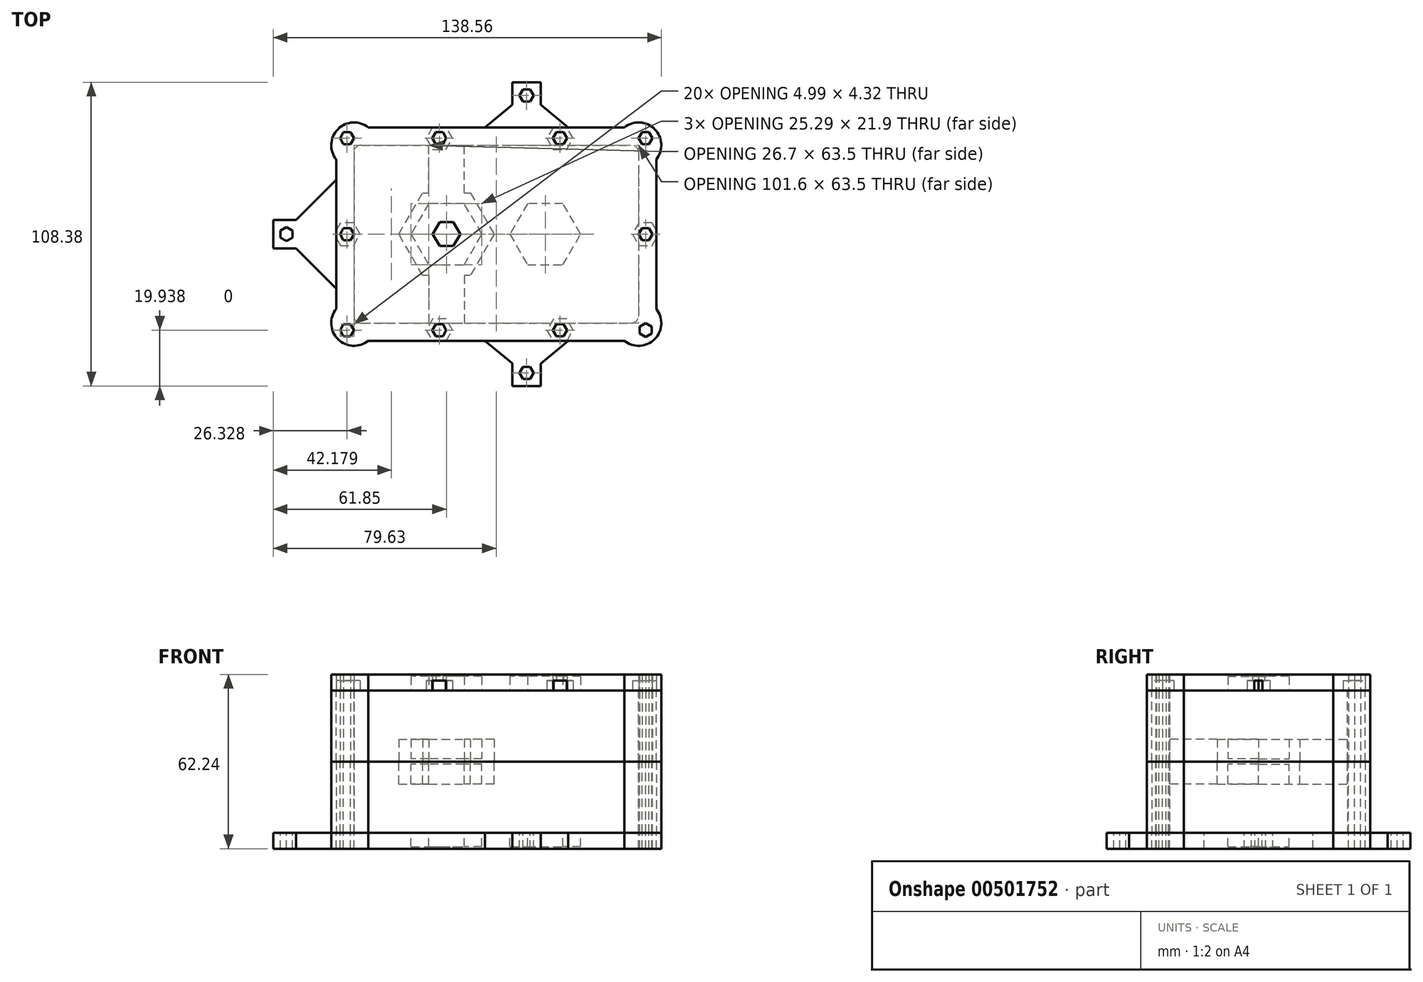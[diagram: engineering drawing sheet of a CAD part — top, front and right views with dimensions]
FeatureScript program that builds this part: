
annotation { "Feature Type Name" : "Feature", "Feature Type Description" : "" }
export const myFeature = defineFeature(function(context is Context, id is Id, definition is map)
    precondition{}
    {
        {
            var Q0;
            Q0=qCreatedBy(makeId("Top.planeOp"),FACE);
            var sketch = newSketch(context, id + "F0", { "sketchPlane" : qUnion([Q0])});
            skLineSegment(sketch, "E0.bottom", {"start": v(-48.26, 31.75) * mm, "end": v(48.26, 31.75) * mm});
            skLineSegment(sketch, "E0.top", {"start": v(-48.26, -31.75) * mm, "end": v(48.26, -31.75) * mm});
            skLineSegment(sketch, "E0.left", {"start": v(-50.8, 29.21) * mm, "end": v(-50.8, -29.21) * mm});
            skLineSegment(sketch, "E0.right", {"start": v(50.8, 29.21) * mm, "end": v(50.8, -29.21) * mm});
            skLineSegment(sketch, "E1", {"start": v(0, 0) * mm, "end": v(0, 31.75) * mm, "construction": true});
            skLineSegment(sketch, "E2", {"start": v(0, 0) * mm, "end": v(-50.8, 0) * mm, "construction": true});
            skLineSegment(sketch, "E3.0", {"start": v(57.15, 26.68) * mm, "end": v(57.15, -26.68) * mm});
            skLineSegment(sketch, "E3.1", {"start": v(-45.73, 38.1) * mm, "end": v(45.73, 38.1) * mm});
            skLineSegment(sketch, "E3.2", {"start": v(-57.15, 26.68) * mm, "end": v(-57.15, -26.68) * mm});
            skLineSegment(sketch, "E3.3", {"start": v(-45.73, -38.1) * mm, "end": v(45.73, -38.1) * mm});
            skPoint(sketch, "E4.visualSharp", {"position": v(-50.8, 31.75) * mm});
            skArc(sketch, "E4.filletArc", {"start": v(-48.26, 31.75) * mm, "mid": v(-50.06, 31) * mm, "end": v(-50.8, 29.21) * mm});
            skPoint(sketch, "E5.visualSharp", {"position": v(-57.15, 38.1) * mm});
            skPoint(sketch, "E6.visualSharp", {"position": v(50.8, 31.75) * mm});
            skArc(sketch, "E6.filletArc", {"start": v(50.8, 29.21) * mm, "mid": v(50.06, 31) * mm, "end": v(48.26, 31.75) * mm});
            skPoint(sketch, "E7.visualSharp", {"position": v(57.15, 38.1) * mm});
            skPoint(sketch, "E8.visualSharp", {"position": v(57.15, -38.1) * mm});
            skPoint(sketch, "E9.visualSharp", {"position": v(50.8, -31.75) * mm});
            skArc(sketch, "E9.filletArc", {"start": v(48.26, -31.75) * mm, "mid": v(50.06, -31) * mm, "end": v(50.8, -29.21) * mm});
            skPoint(sketch, "E10.visualSharp", {"position": v(-50.8, -31.75) * mm});
            skArc(sketch, "E10.filletArc", {"start": v(-50.8, -29.21) * mm, "mid": v(-50.06, -31) * mm, "end": v(-48.26, -31.75) * mm});
            skPoint(sketch, "E11.visualSharp", {"position": v(-57.15, -38.1) * mm});
            skArc(sketch, "E12", {"start": v(-57.15, -26.68) * mm, "mid": v(-56.55, -37.5) * mm, "end": v(-45.73, -38.1) * mm});
            skArc(sketch, "E13", {"start": v(45.73, -38.1) * mm, "mid": v(56.55, -37.5) * mm, "end": v(57.15, -26.68) * mm});
            skArc(sketch, "E14", {"start": v(57.15, 26.68) * mm, "mid": v(56.55, 37.5) * mm, "end": v(45.73, 38.1) * mm});
            skArc(sketch, "E15", {"start": v(-45.73, 38.1) * mm, "mid": v(-56.55, 37.5) * mm, "end": v(-57.15, 26.68) * mm});
            skSolve(sketch);
        }
        {
            var Q0;
            Q0=makeQuery(id+"F0.imprint","IMPRINT",FACE,{"disambiguationData":[TD([[makeQuery(id+"F0.imprint","IMPRINT",EDGE,{"derivedFrom":sQuery(id+"F0.wireOp",EDGE,"E0.bottom")}),1.0]])]});
            var Q1;
            {var subQ0=sQuery(id+"F0.wireOp",EDGE,"E11.filletArc");Q1=makeQuery(id+"F0.imprint","IMPRINT",FACE,{"disambiguationData":[TD([[makeQuery(id+"F0.imprint","IMPRINT",EDGE,{"derivedFrom":subQ0}),-1.0]])]});}
            var Q2;
            {var subQ0=sQuery(id+"F0.wireOp",EDGE,"E8.filletArc");Q2=makeQuery(id+"F0.imprint","IMPRINT",FACE,{"disambiguationData":[TD([[makeQuery(id+"F0.imprint","IMPRINT",EDGE,{"derivedFrom":subQ0}),-1.0]])]});}
            var Q3;
            {var subQ0=sQuery(id+"F0.wireOp",EDGE,"E7.filletArc");Q3=makeQuery(id+"F0.imprint","IMPRINT",FACE,{"disambiguationData":[TD([[makeQuery(id+"F0.imprint","IMPRINT",EDGE,{"derivedFrom":subQ0}),-1.0]])]});}
            var Q4;
            {var subQ0=sQuery(id+"F0.wireOp",EDGE,"E5.filletArc");Q4=makeQuery(id+"F0.imprint","IMPRINT",FACE,{"disambiguationData":[TD([[makeQuery(id+"F0.imprint","IMPRINT",EDGE,{"derivedFrom":subQ0}),-1.0]])]});}
            extrude(context, id + "F1", {"entities" : qUnion([Q0, Q1, Q2, Q3, Q4]), "depth" : 25.4 * mm});
        }
        {
            var Q0;
            Q0=makeQuery(id+"F1.opExtrude","CAP_FACE",FACE,{"disambiguationData":[OSD([sQuery(id+"F0.wireOp",EDGE,"E0.bottom"),sQuery(id+"F0.wireOp",EDGE,"E0.top"),sQuery(id+"F0.wireOp",EDGE,"E0.left"),sQuery(id+"F0.wireOp",EDGE,"E0.right"),sQuery(id+"F0.wireOp",EDGE,"E3.0"),sQuery(id+"F0.wireOp",EDGE,"E3.1"),sQuery(id+"F0.wireOp",EDGE,"E3.2"),sQuery(id+"F0.wireOp",EDGE,"E3.3"),sQuery(id+"F0.wireOp",EDGE,"E4.filletArc"),sQuery(id+"F0.wireOp",EDGE,"E5.filletArc"),sQuery(id+"F0.wireOp",EDGE,"E6.filletArc"),sQuery(id+"F0.wireOp",EDGE,"E7.filletArc"),sQuery(id+"F0.wireOp",EDGE,"E8.filletArc"),sQuery(id+"F0.wireOp",EDGE,"E9.filletArc"),sQuery(id+"F0.wireOp",EDGE,"E10.filletArc"),sQuery(id+"F0.wireOp",EDGE,"E11.filletArc")])],"isStart":true});
            var sketch = newSketch(context, id + "F2", { "sketchPlane" : qUnion([Q0])});
            skCircle(sketch, "E16", {"center": v(-17.78, 0) * mm, "radius": 57.15 * mm, "construction": true});
            skLineSegment(sketch, "E17", {"start": v(-17.78, 0) * mm, "end": v(10.8, -49.5) * mm, "construction": true});
            skLineSegment(sketch, "E18", {"start": v(-17.78, 0) * mm, "end": v(10.8, 49.5) * mm, "construction": true});
            skLineSegment(sketch, "E19", {"start": v(-17.78, 0) * mm, "end": v(-74.93, 0) * mm, "construction": true});
            skCircle(sketch, "E20.cCircle", {"center": v(-17.78, 0) * mm, "radius": 4.25 * mm, "construction": true});
            skLineSegment(sketch, "E20.0", {"start": v(-20.23, 4.25) * mm, "end": v(-15.33, 4.25) * mm});
            skLineSegment(sketch, "E20.1", {"start": v(-15.33, 4.25) * mm, "end": v(-12.87, 0) * mm});
            skLineSegment(sketch, "E20.2", {"start": v(-12.87, 0) * mm, "end": v(-15.33, -4.25) * mm});
            skLineSegment(sketch, "E20.3", {"start": v(-15.33, -4.25) * mm, "end": v(-20.23, -4.25) * mm});
            skLineSegment(sketch, "E20.4", {"start": v(-20.23, -4.25) * mm, "end": v(-22.69, 0) * mm});
            skLineSegment(sketch, "E20.5", {"start": v(-22.69, 0) * mm, "end": v(-20.23, 4.25) * mm});
            skPoint(sketch, "E20.0.midPoint", {"position": v(-17.78, 4.25) * mm});
            skCircle(sketch, "E21.cCircle", {"center": v(-74.93, 0) * mm, "radius": 2.16 * mm, "construction": true});
            skLineSegment(sketch, "E21.0", {"start": v(-77.09, -1.25) * mm, "end": v(-77.09, 1.25) * mm});
            skLineSegment(sketch, "E21.1", {"start": v(-77.09, 1.25) * mm, "end": v(-74.93, 2.5) * mm});
            skLineSegment(sketch, "E21.2", {"start": v(-74.93, 2.5) * mm, "end": v(-72.77, 1.25) * mm});
            skLineSegment(sketch, "E21.3", {"start": v(-72.77, 1.25) * mm, "end": v(-72.77, -1.25) * mm});
            skLineSegment(sketch, "E21.4", {"start": v(-72.77, -1.25) * mm, "end": v(-74.93, -2.5) * mm});
            skLineSegment(sketch, "E21.5", {"start": v(-74.93, -2.5) * mm, "end": v(-77.09, -1.25) * mm});
            skPoint(sketch, "E21.0.midPoint", {"position": v(-77.09, 0) * mm});
            skPoint(sketch, "E22", {"position": v(-57.15, 0) * mm});
            skCircle(sketch, "E23.cCircle", {"center": v(10.8, 49.5) * mm, "radius": 2.16 * mm, "construction": true});
            skLineSegment(sketch, "E23.0", {"start": v(9.55, 51.65) * mm, "end": v(12.04, 51.65) * mm});
            skLineSegment(sketch, "E23.1", {"start": v(12.04, 51.65) * mm, "end": v(13.29, 49.5) * mm});
            skLineSegment(sketch, "E23.2", {"start": v(13.29, 49.5) * mm, "end": v(12.04, 47.33) * mm});
            skLineSegment(sketch, "E23.3", {"start": v(12.04, 47.33) * mm, "end": v(9.55, 47.33) * mm});
            skLineSegment(sketch, "E23.4", {"start": v(9.55, 47.33) * mm, "end": v(8.3, 49.5) * mm});
            skLineSegment(sketch, "E23.5", {"start": v(8.3, 49.5) * mm, "end": v(9.55, 51.65) * mm});
            skPoint(sketch, "E23.0.midPoint", {"position": v(10.8, 51.65) * mm});
            skCircle(sketch, "E24.cCircle", {"center": v(10.8, -49.5) * mm, "radius": 2.16 * mm, "construction": true});
            skLineSegment(sketch, "E24.0", {"start": v(12.04, -51.65) * mm, "end": v(9.55, -51.65) * mm});
            skLineSegment(sketch, "E24.1", {"start": v(9.55, -51.65) * mm, "end": v(8.3, -49.5) * mm});
            skLineSegment(sketch, "E24.2", {"start": v(8.3, -49.5) * mm, "end": v(9.55, -47.33) * mm});
            skLineSegment(sketch, "E24.3", {"start": v(9.55, -47.33) * mm, "end": v(12.04, -47.33) * mm});
            skLineSegment(sketch, "E24.4", {"start": v(12.04, -47.33) * mm, "end": v(13.29, -49.5) * mm});
            skLineSegment(sketch, "E24.5", {"start": v(13.29, -49.5) * mm, "end": v(12.04, -51.65) * mm});
            skPoint(sketch, "E24.0.midPoint", {"position": v(10.8, -51.65) * mm});
            skLineSegment(sketch, "E25.bottom", {"start": v(-79.63, -5.08) * mm, "end": v(-57.15, -5.08) * mm});
            skLineSegment(sketch, "E25.top", {"start": v(-79.63, 5.08) * mm, "end": v(-57.15, 5.08) * mm});
            skLineSegment(sketch, "E25.left", {"start": v(-79.63, -5.08) * mm, "end": v(-79.63, 5.08) * mm});
            skLineSegment(sketch, "E25.right", {"start": v(-57.15, -5.08) * mm, "end": v(-57.15, 5.08) * mm});
            skLineSegment(sketch, "E26.bottom", {"start": v(5.71, -54.2) * mm, "end": v(15.87, -54.2) * mm});
            skLineSegment(sketch, "E26.top", {"start": v(5.71, -38.1) * mm, "end": v(15.87, -38.1) * mm});
            skLineSegment(sketch, "E26.left", {"start": v(5.71, -54.2) * mm, "end": v(5.71, -38.1) * mm});
            skLineSegment(sketch, "E26.right", {"start": v(15.87, -54.2) * mm, "end": v(15.87, -38.1) * mm});
            skLineSegment(sketch, "E27.bottom", {"start": v(5.72, 38.1) * mm, "end": v(15.88, 38.1) * mm});
            skLineSegment(sketch, "E27.top", {"start": v(5.72, 54.2) * mm, "end": v(15.88, 54.2) * mm});
            skLineSegment(sketch, "E27.left", {"start": v(5.72, 38.1) * mm, "end": v(5.72, 54.2) * mm});
            skLineSegment(sketch, "E27.right", {"start": v(15.88, 38.1) * mm, "end": v(15.88, 54.2) * mm});
            skLineSegment(sketch, "E28", {"start": v(10.8, 49.5) * mm, "end": v(10.8, 54.2) * mm, "construction": true});
            skLineSegment(sketch, "E29", {"start": v(10.8, -54.2) * mm, "end": v(10.8, -49.5) * mm, "construction": true});
            skLineSegment(sketch, "E30", {"start": v(-79.63, 0) * mm, "end": v(-77.09, 0) * mm, "construction": true});
            skLineSegment(sketch, "E31", {"start": v(5.72, 46.15) * mm, "end": v(-4.11, 38.1) * mm});
            skLineSegment(sketch, "E32", {"start": v(15.88, 46.19) * mm, "end": v(25.67, 38.1) * mm});
            skPoint(sketch, "E33", {"position": v(15.88, 46.15) * mm});
            skLineSegment(sketch, "E34", {"start": v(15.87, -46.15) * mm, "end": v(25.7, -38.1) * mm});
            skLineSegment(sketch, "E35", {"start": v(5.71, -46.15) * mm, "end": v(-4.11, -38.1) * mm});
            skLineSegment(sketch, "E36", {"start": v(-71.52, -5.08) * mm, "end": v(-57.15, -19.45) * mm});
            skLineSegment(sketch, "E37", {"start": v(-71.52, 5.08) * mm, "end": v(-57.15, 19.45) * mm});
            skCircle(sketch, "E38.cCircle", {"center": v(17.5, 0) * mm, "radius": 4.25 * mm, "construction": true});
            skLineSegment(sketch, "E38.0", {"start": v(15.04, 4.25) * mm, "end": v(19.95, 4.25) * mm});
            skLineSegment(sketch, "E38.1", {"start": v(19.95, 4.25) * mm, "end": v(22.4, 0) * mm});
            skLineSegment(sketch, "E38.2", {"start": v(22.4, 0) * mm, "end": v(19.95, -4.25) * mm});
            skLineSegment(sketch, "E38.3", {"start": v(19.95, -4.25) * mm, "end": v(15.04, -4.25) * mm});
            skLineSegment(sketch, "E38.4", {"start": v(15.04, -4.25) * mm, "end": v(12.59, 0) * mm});
            skLineSegment(sketch, "E38.5", {"start": v(12.59, 0) * mm, "end": v(15.04, 4.25) * mm});
            skPoint(sketch, "E38.0.midPoint", {"position": v(17.5, 4.25) * mm});
            skSolve(sketch);
        }
        {
            var Q0;
            {var subQ3=sQuery(id+"F2.wireOp",EDGE,"E37");Q0=makeQuery(id+"F2.imprint","IMPRINT",FACE,{"disambiguationData":[TD([[makeQuery(id+"F2.imprint","IMPRINT",EDGE,{"derivedFrom":subQ3}),-1.0]])]});}
            var Q1;
            Q1=makeQuery(id+"F2.imprint","IMPRINT",FACE,{"disambiguationData":[TD([[makeQuery(id+"F2.imprint","IMPRINT",EDGE,{"derivedFrom":sQuery(id+"F2.wireOp",EDGE,"E21.0")}),1.0]])]});
            var Q2;
            {var subQ3=sQuery(id+"F2.wireOp",EDGE,"E36");Q2=makeQuery(id+"F2.imprint","IMPRINT",FACE,{"disambiguationData":[TD([[makeQuery(id+"F2.imprint","IMPRINT",EDGE,{"derivedFrom":subQ3}),1.0]])]});}
            var Q3;
            {var subQ14=sQuery(id+"F2.wireOp",EDGE,"E25.right");Q3=makeQuery(id+"F2.imprint","IMPRINT",FACE,{"disambiguationData":[TD([[makeQuery(id+"F2.imprint","IMPRINT",EDGE,{"derivedFrom":subQ14}),-1.0]])]});}
            var Q4;
            Q4=makeQuery(id+"F2.imprint","IMPRINT",FACE,{"disambiguationData":[TD([[makeQuery(id+"F2.imprint","IMPRINT",EDGE,{"derivedFrom":sQuery(id+"F2.wireOp",EDGE,"E20.0")}),1.0]])]});
            var Q5;
            Q5=makeQuery(id+"F2.imprint","IMPRINT",FACE,{"disambiguationData":[TD([[makeQuery(id+"F2.imprint","IMPRINT",EDGE,{"derivedFrom":sQuery(id+"F2.wireOp",EDGE,"E23.0")}),1.0]])]});
            var Q6;
            {var subQ3=sQuery(id+"F2.wireOp",EDGE,"E31");Q6=makeQuery(id+"F2.imprint","IMPRINT",FACE,{"disambiguationData":[TD([[makeQuery(id+"F2.imprint","IMPRINT",EDGE,{"derivedFrom":subQ3}),1.0]])]});}
            var Q7;
            {var subQ3=sQuery(id+"F2.wireOp",EDGE,"E32");Q7=makeQuery(id+"F2.imprint","IMPRINT",FACE,{"disambiguationData":[TD([[makeQuery(id+"F2.imprint","IMPRINT",EDGE,{"derivedFrom":subQ3}),-1.0]])]});}
            var Q8;
            {var subQ3=sQuery(id+"F2.wireOp",EDGE,"E35");Q8=makeQuery(id+"F2.imprint","IMPRINT",FACE,{"disambiguationData":[TD([[makeQuery(id+"F2.imprint","IMPRINT",EDGE,{"derivedFrom":subQ3}),-1.0]])]});}
            var Q9;
            Q9=makeQuery(id+"F2.imprint","IMPRINT",FACE,{"disambiguationData":[TD([[makeQuery(id+"F2.imprint","IMPRINT",EDGE,{"derivedFrom":sQuery(id+"F2.wireOp",EDGE,"E24.0")}),1.0]])]});
            var Q10;
            {var subQ3=sQuery(id+"F2.wireOp",EDGE,"E34");Q10=makeQuery(id+"F2.imprint","IMPRINT",FACE,{"disambiguationData":[TD([[makeQuery(id+"F2.imprint","IMPRINT",EDGE,{"derivedFrom":subQ3}),1.0]])]});}
            var Q11;
            Q11=makeQuery(id+"F2.imprint","IMPRINT",FACE,{"disambiguationData":[TD([[makeQuery(id+"F2.imprint","IMPRINT",EDGE,{"derivedFrom":sQuery(id+"F2.wireOp",EDGE,"E38.0")}),-1.0]])]});
            extrude(context, id + "F3", {"entities" : qUnion([Q0, Q1, Q2, Q3, Q4, Q5, Q6, Q7, Q8, Q9, Q10, Q11]), "depth" : 5.7 * mm});
        }
        {
            var Q0;
            {var subQ0=sQuery(id+"F2.wireOp",EDGE,"E20.0");var subQ1=sQuery(id+"F2.wireOp",EDGE,"E38.5");var subQ2=sQuery(id+"F2.wireOp",EDGE,"E20.4");var subQ3=sQuery(id+"F2.wireOp",EDGE,"E20.5");var subQ4=sQuery(id+"F2.wireOp",EDGE,"E38.1");var subQ5=sQuery(id+"F2.wireOp",EDGE,"E38.4");var subQ6=sQuery(id+"F2.wireOp",EDGE,"E20.1");var subQ7=sQuery(id+"F2.wireOp",EDGE,"E20.2");var subQ8=sQuery(id+"F2.wireOp",EDGE,"E20.3");var subQ9=sQuery(id+"F2.wireOp",EDGE,"E38.0");var subQ10=sQuery(id+"F2.wireOp",EDGE,"E38.2");var subQ11=sQuery(id+"F2.wireOp",EDGE,"E38.3");Q0=makeQuery(id+"F3.boolean.opBoolean","SPLIT",FACE,{"disambiguationData":[TD([makeQuery(id+"F1.opExtrude","SWEPT_FACE",FACE,{"disambiguationData":[OSD([sQuery(id+"F0.wireOp",EDGE,"E0.bottom")])]})])],"derivedFrom":makeQuery(id+"F3.opExtrude","CAP_FACE",FACE,{"disambiguationData":[OSD([sQuery(id+"F0.wireOp",EDGE,"E3.0"),sQuery(id+"F0.wireOp",EDGE,"E3.1"),sQuery(id+"F0.wireOp",EDGE,"E3.2"),sQuery(id+"F0.wireOp",EDGE,"E3.3"),sQuery(id+"F0.wireOp",EDGE,"E12"),sQuery(id+"F0.wireOp",EDGE,"E13"),sQuery(id+"F0.wireOp",EDGE,"E14"),sQuery(id+"F0.wireOp",EDGE,"E15"),subQ0,subQ6,subQ7,subQ8,subQ2,subQ3,sQuery(id+"F2.wireOp",EDGE,"E21.0"),sQuery(id+"F2.wireOp",EDGE,"E21.1"),sQuery(id+"F2.wireOp",EDGE,"E21.2"),sQuery(id+"F2.wireOp",EDGE,"E21.3"),sQuery(id+"F2.wireOp",EDGE,"E21.4"),sQuery(id+"F2.wireOp",EDGE,"E21.5"),sQuery(id+"F2.wireOp",EDGE,"E23.0"),sQuery(id+"F2.wireOp",EDGE,"E23.1"),sQuery(id+"F2.wireOp",EDGE,"E23.2"),sQuery(id+"F2.wireOp",EDGE,"E23.3"),sQuery(id+"F2.wireOp",EDGE,"E23.4"),sQuery(id+"F2.wireOp",EDGE,"E23.5"),sQuery(id+"F2.wireOp",EDGE,"E24.0"),sQuery(id+"F2.wireOp",EDGE,"E24.1"),sQuery(id+"F2.wireOp",EDGE,"E24.2"),sQuery(id+"F2.wireOp",EDGE,"E24.3"),sQuery(id+"F2.wireOp",EDGE,"E24.4"),sQuery(id+"F2.wireOp",EDGE,"E24.5"),sQuery(id+"F2.wireOp",EDGE,"E25.bottom"),sQuery(id+"F2.wireOp",EDGE,"E25.top"),sQuery(id+"F2.wireOp",EDGE,"E25.left"),sQuery(id+"F2.wireOp",EDGE,"E26.bottom"),sQuery(id+"F2.wireOp",EDGE,"E26.left"),sQuery(id+"F2.wireOp",EDGE,"E26.right"),sQuery(id+"F2.wireOp",EDGE,"E27.top"),sQuery(id+"F2.wireOp",EDGE,"E27.left"),sQuery(id+"F2.wireOp",EDGE,"E27.right"),sQuery(id+"F2.wireOp",EDGE,"E31"),sQuery(id+"F2.wireOp",EDGE,"E32"),sQuery(id+"F2.wireOp",EDGE,"E34"),sQuery(id+"F2.wireOp",EDGE,"E35"),sQuery(id+"F2.wireOp",EDGE,"E36"),sQuery(id+"F2.wireOp",EDGE,"E37"),subQ9,subQ4,subQ10,subQ11,subQ5,subQ1])],"isStart":true})});}
            var sketch = newSketch(context, id + "F4", { "sketchPlane" : qUnion([Q0])});
            skPoint(sketch, "E39.0", {"position": v(-17.78, 0) * mm});
            skPoint(sketch, "E39.1", {"position": v(17.5, 0) * mm});
            skCircle(sketch, "E40.cCircle", {"center": v(-17.78, 0) * mm, "radius": 10.95 * mm, "construction": true});
            skLineSegment(sketch, "E40.0", {"start": v(-24.1, 10.95) * mm, "end": v(-11.46, 10.95) * mm});
            skLineSegment(sketch, "E40.1", {"start": v(-11.46, 10.95) * mm, "end": v(-5.14, 0) * mm});
            skLineSegment(sketch, "E40.2", {"start": v(-5.14, 0) * mm, "end": v(-11.46, -10.95) * mm});
            skLineSegment(sketch, "E40.3", {"start": v(-11.46, -10.95) * mm, "end": v(-24.1, -10.95) * mm});
            skLineSegment(sketch, "E40.4", {"start": v(-24.1, -10.95) * mm, "end": v(-30.42, 0) * mm});
            skLineSegment(sketch, "E40.5", {"start": v(-30.42, 0) * mm, "end": v(-24.1, 10.95) * mm});
            skPoint(sketch, "E40.0.midPoint", {"position": v(-17.78, 10.95) * mm});
            skCircle(sketch, "E41.cCircle", {"center": v(17.5, 0) * mm, "radius": 10.95 * mm, "construction": true});
            skLineSegment(sketch, "E41.0", {"start": v(11.17, 10.95) * mm, "end": v(23.82, 10.95) * mm});
            skLineSegment(sketch, "E41.1", {"start": v(23.82, 10.95) * mm, "end": v(30.14, 0) * mm});
            skLineSegment(sketch, "E41.2", {"start": v(30.14, 0) * mm, "end": v(23.82, -10.95) * mm});
            skLineSegment(sketch, "E41.3", {"start": v(23.82, -10.95) * mm, "end": v(11.17, -10.95) * mm});
            skLineSegment(sketch, "E41.4", {"start": v(11.17, -10.95) * mm, "end": v(4.85, 0) * mm});
            skLineSegment(sketch, "E41.5", {"start": v(4.85, 0) * mm, "end": v(11.17, 10.95) * mm});
            skPoint(sketch, "E41.0.midPoint", {"position": v(17.5, 10.95) * mm});
            skSolve(sketch);
        }
        {
            var Q0;
            Q0=makeQuery(id+"F4.imprint","IMPRINT",FACE,{"disambiguationData":[TD([[makeQuery(id+"F4.imprint","IMPRINT",EDGE,{"derivedFrom":sQuery(id+"F4.wireOp",EDGE,"E40.0")}),-1.0]])]});
            var Q1;
            Q1=makeQuery(id+"F4.imprint","IMPRINT",FACE,{"disambiguationData":[TD([[makeQuery(id+"F4.imprint","IMPRINT",EDGE,{"derivedFrom":sQuery(id+"F4.wireOp",EDGE,"E41.0")}),-1.0]])]});
            extrude(context, id + "F5", {"entities" : qUnion([Q0, Q1]), "operationType" : NewBodyOperationType.REMOVE, "oppositeDirection" : true, "depth" : 5 * mm});
        }
        {
            var Q0;
            Q0=makeQuery(id+"F1.opExtrude","CAP_FACE",FACE,{"disambiguationData":[OSD([sQuery(id+"F0.wireOp",EDGE,"E0.bottom"),sQuery(id+"F0.wireOp",EDGE,"E0.top"),sQuery(id+"F0.wireOp",EDGE,"E0.left"),sQuery(id+"F0.wireOp",EDGE,"E0.right"),sQuery(id+"F0.wireOp",EDGE,"E3.0"),sQuery(id+"F0.wireOp",EDGE,"E3.1"),sQuery(id+"F0.wireOp",EDGE,"E3.2"),sQuery(id+"F0.wireOp",EDGE,"E3.3"),sQuery(id+"F0.wireOp",EDGE,"E4.filletArc"),sQuery(id+"F0.wireOp",EDGE,"E6.filletArc"),sQuery(id+"F0.wireOp",EDGE,"E9.filletArc"),sQuery(id+"F0.wireOp",EDGE,"E10.filletArc"),sQuery(id+"F0.wireOp",EDGE,"E12"),sQuery(id+"F0.wireOp",EDGE,"E13"),sQuery(id+"F0.wireOp",EDGE,"E14"),sQuery(id+"F0.wireOp",EDGE,"E15")])],"isStart":false});
            var sketch = newSketch(context, id + "F6", { "sketchPlane" : qUnion([Q0])});
            skLineSegment(sketch, "E42", {"start": v(-56.55, 37.5) * mm, "end": v(-50.06, 31) * mm, "construction": true});
            skLineSegment(sketch, "E43", {"start": v(50.06, 31) * mm, "end": v(56.55, 37.5) * mm, "construction": true});
            skLineSegment(sketch, "E44", {"start": v(56.55, -37.5) * mm, "end": v(50.06, -31) * mm, "construction": true});
            skLineSegment(sketch, "E45", {"start": v(-50.06, -31) * mm, "end": v(-56.55, -37.5) * mm, "construction": true});
            skCircle(sketch, "E46.cCircle", {"center": v(-53.3, 34.25) * mm, "radius": 2.16 * mm, "construction": true});
            skLineSegment(sketch, "E46.0", {"start": v(-54.55, 36.41) * mm, "end": v(-52.06, 36.41) * mm});
            skLineSegment(sketch, "E46.1", {"start": v(-52.06, 36.41) * mm, "end": v(-50.8, 34.25) * mm});
            skLineSegment(sketch, "E46.2", {"start": v(-50.8, 34.25) * mm, "end": v(-52.06, 32.1) * mm});
            skLineSegment(sketch, "E46.3", {"start": v(-52.06, 32.1) * mm, "end": v(-54.55, 32.1) * mm});
            skLineSegment(sketch, "E46.4", {"start": v(-54.55, 32.1) * mm, "end": v(-55.8, 34.25) * mm});
            skLineSegment(sketch, "E46.5", {"start": v(-55.8, 34.25) * mm, "end": v(-54.55, 36.41) * mm});
            skPoint(sketch, "E46.0.midPoint", {"position": v(-53.3, 36.41) * mm});
            skCircle(sketch, "E47.cCircle", {"center": v(53.3, 34.25) * mm, "radius": 2.16 * mm, "construction": true});
            skLineSegment(sketch, "E47.0", {"start": v(52.06, 36.41) * mm, "end": v(54.55, 36.41) * mm});
            skLineSegment(sketch, "E47.1", {"start": v(54.55, 36.41) * mm, "end": v(55.8, 34.25) * mm});
            skLineSegment(sketch, "E47.2", {"start": v(55.8, 34.25) * mm, "end": v(54.55, 32.1) * mm});
            skLineSegment(sketch, "E47.3", {"start": v(54.55, 32.1) * mm, "end": v(52.06, 32.1) * mm});
            skLineSegment(sketch, "E47.4", {"start": v(52.06, 32.1) * mm, "end": v(50.8, 34.25) * mm});
            skLineSegment(sketch, "E47.5", {"start": v(50.8, 34.25) * mm, "end": v(52.06, 36.41) * mm});
            skPoint(sketch, "E47.0.midPoint", {"position": v(53.3, 36.41) * mm});
            skCircle(sketch, "E48.cCircle", {"center": v(53.3, -34.25) * mm, "radius": 2.16 * mm, "construction": true});
            skLineSegment(sketch, "E48.0", {"start": v(55.46, -33) * mm, "end": v(55.46, -35.5) * mm});
            skLineSegment(sketch, "E48.1", {"start": v(55.46, -35.5) * mm, "end": v(53.3, -36.74) * mm});
            skLineSegment(sketch, "E48.2", {"start": v(53.3, -36.74) * mm, "end": v(51.14, -35.5) * mm});
            skLineSegment(sketch, "E48.3", {"start": v(51.14, -35.5) * mm, "end": v(51.14, -33) * mm});
            skLineSegment(sketch, "E48.4", {"start": v(51.14, -33) * mm, "end": v(53.3, -31.76) * mm});
            skLineSegment(sketch, "E48.5", {"start": v(53.3, -31.76) * mm, "end": v(55.46, -33) * mm});
            skPoint(sketch, "E48.0.midPoint", {"position": v(55.46, -34.25) * mm});
            skCircle(sketch, "E49.cCircle", {"center": v(-53.3, -34.25) * mm, "radius": 2.16 * mm, "construction": true});
            skLineSegment(sketch, "E49.0", {"start": v(-54.55, -32.1) * mm, "end": v(-52.06, -32.1) * mm});
            skLineSegment(sketch, "E49.1", {"start": v(-52.06, -32.1) * mm, "end": v(-50.8, -34.25) * mm});
            skLineSegment(sketch, "E49.2", {"start": v(-50.8, -34.25) * mm, "end": v(-52.06, -36.41) * mm});
            skLineSegment(sketch, "E49.3", {"start": v(-52.06, -36.41) * mm, "end": v(-54.55, -36.41) * mm});
            skLineSegment(sketch, "E49.4", {"start": v(-54.55, -36.41) * mm, "end": v(-55.8, -34.25) * mm});
            skLineSegment(sketch, "E49.5", {"start": v(-55.8, -34.25) * mm, "end": v(-54.55, -32.1) * mm});
            skPoint(sketch, "E49.0.midPoint", {"position": v(-53.3, -32.1) * mm});
            skSolve(sketch);
        }
        {
            var Q0;
            Q0=makeQuery(id+"F6.imprint","IMPRINT",FACE,{"disambiguationData":[TD([[makeQuery(id+"F6.imprint","IMPRINT",EDGE,{"derivedFrom":sQuery(id+"F6.wireOp",EDGE,"E46.0")}),-1.0]])]});
            var Q1;
            Q1=makeQuery(id+"F6.imprint","IMPRINT",FACE,{"disambiguationData":[TD([[makeQuery(id+"F6.imprint","IMPRINT",EDGE,{"derivedFrom":sQuery(id+"F6.wireOp",EDGE,"E47.0")}),-1.0]])]});
            var Q2;
            Q2=makeQuery(id+"F6.imprint","IMPRINT",FACE,{"disambiguationData":[TD([[makeQuery(id+"F6.imprint","IMPRINT",EDGE,{"derivedFrom":sQuery(id+"F6.wireOp",EDGE,"E48.0")}),-1.0]])]});
            var Q3;
            Q3=makeQuery(id+"F6.imprint","IMPRINT",FACE,{"disambiguationData":[TD([[makeQuery(id+"F6.imprint","IMPRINT",EDGE,{"derivedFrom":sQuery(id+"F6.wireOp",EDGE,"E49.0")}),-1.0]])]});
            extrude(context, id + "F7", {"entities" : qUnion([Q0, Q1, Q2, Q3]), "operationType" : NewBodyOperationType.REMOVE, "endBound" : BoundingType.THROUGH_ALL, "oppositeDirection" : true, "depth" : 25.4 * mm});
        }
        {
            var Q0;
            Q0=makeQuery(id+"F1.opExtrude","CAP_FACE",FACE,{"disambiguationData":[OSD([sQuery(id+"F0.wireOp",EDGE,"E0.bottom"),sQuery(id+"F0.wireOp",EDGE,"E0.top"),sQuery(id+"F0.wireOp",EDGE,"E0.left"),sQuery(id+"F0.wireOp",EDGE,"E0.right"),sQuery(id+"F0.wireOp",EDGE,"E3.0"),sQuery(id+"F0.wireOp",EDGE,"E3.1"),sQuery(id+"F0.wireOp",EDGE,"E3.2"),sQuery(id+"F0.wireOp",EDGE,"E3.3"),sQuery(id+"F0.wireOp",EDGE,"E4.filletArc"),sQuery(id+"F0.wireOp",EDGE,"E6.filletArc"),sQuery(id+"F0.wireOp",EDGE,"E9.filletArc"),sQuery(id+"F0.wireOp",EDGE,"E10.filletArc"),sQuery(id+"F0.wireOp",EDGE,"E12"),sQuery(id+"F0.wireOp",EDGE,"E13"),sQuery(id+"F0.wireOp",EDGE,"E14"),sQuery(id+"F0.wireOp",EDGE,"E15")])],"isStart":false});
            var sketch = newSketch(context, id + "F8", { "sketchPlane" : qUnion([Q0])});
            skLineSegment(sketch, "E50.0", {"start": v(-11.46, -10.95) * mm, "end": v(-24.1, -10.95) * mm});
            skLineSegment(sketch, "E50.1", {"start": v(-5.14, 0) * mm, "end": v(-11.46, -10.95) * mm});
            skLineSegment(sketch, "E50.2", {"start": v(-11.46, 10.95) * mm, "end": v(-5.14, 0) * mm});
            skLineSegment(sketch, "E50.3", {"start": v(-24.1, 10.95) * mm, "end": v(-11.46, 10.95) * mm});
            skLineSegment(sketch, "E50.4", {"start": v(-30.42, 0) * mm, "end": v(-24.1, 10.95) * mm});
            skLineSegment(sketch, "E50.5", {"start": v(-24.1, -10.95) * mm, "end": v(-30.42, 0) * mm});
            skLineSegment(sketch, "E51.bottom", {"start": v(-24.1, 14.76) * mm, "end": v(-11.46, 14.76) * mm});
            skLineSegment(sketch, "E51.top", {"start": v(-24.1, 31.75) * mm, "end": v(-11.46, 31.75) * mm});
            skLineSegment(sketch, "E51.left", {"start": v(-24.1, 14.76) * mm, "end": v(-24.1, 31.75) * mm});
            skLineSegment(sketch, "E51.right", {"start": v(-11.46, 14.76) * mm, "end": v(-11.46, 31.75) * mm});
            skLineSegment(sketch, "E52.top", {"start": v(-11.46, -31.75) * mm, "end": v(-24.1, -31.75) * mm});
            skLineSegment(sketch, "E52.left", {"start": v(-11.46, -14.76) * mm, "end": v(-11.46, -31.75) * mm});
            skLineSegment(sketch, "E52.right", {"start": v(-24.1, -14.76) * mm, "end": v(-24.1, -31.75) * mm});
            skPoint(sketch, "E53.0", {"position": v(-17.78, 0) * mm});
            skCircle(sketch, "E54.cCircle", {"center": v(-17.78, 0) * mm, "radius": 14.76 * mm, "construction": true});
            skLineSegment(sketch, "E54.0", {"start": v(-26.3, 14.76) * mm, "end": v(-9.26, 14.76) * mm});
            skLineSegment(sketch, "E54.1", {"start": v(-9.26, 14.76) * mm, "end": v(-0.74, 0) * mm});
            skLineSegment(sketch, "E54.2", {"start": v(-0.74, 0) * mm, "end": v(-9.26, -14.76) * mm});
            skLineSegment(sketch, "E54.3", {"start": v(-9.26, -14.76) * mm, "end": v(-26.3, -14.76) * mm});
            skLineSegment(sketch, "E54.4", {"start": v(-26.3, -14.76) * mm, "end": v(-34.82, 0) * mm});
            skLineSegment(sketch, "E54.5", {"start": v(-34.82, 0) * mm, "end": v(-26.3, 14.76) * mm});
            skPoint(sketch, "E54.0.midPoint", {"position": v(-17.78, 14.76) * mm});
            skSolve(sketch);
        }
        {
            var Q0;
            Q0=makeQuery(id+"F8.imprint","IMPRINT",FACE,{"disambiguationData":[TD([[makeQuery(id+"F8.imprint","IMPRINT",EDGE,{"derivedFrom":sQuery(id+"F8.wireOp",EDGE,"E51.top")}),-1.0]])]});
            var Q1;
            Q1=makeQuery(id+"F8.imprint","IMPRINT",FACE,{"disambiguationData":[TD([[makeQuery(id+"F8.imprint","IMPRINT",EDGE,{"derivedFrom":sQuery(id+"F8.wireOp",EDGE,"E50.0")}),1.0]])]});
            var Q2;
            Q2=makeQuery(id+"F8.imprint","IMPRINT",FACE,{"disambiguationData":[TD([[makeQuery(id+"F8.imprint","IMPRINT",EDGE,{"derivedFrom":sQuery(id+"F8.wireOp",EDGE,"E52.top")}),1.0]])]});
            extrude(context, id + "F9", {"entities" : qUnion([Q0, Q1, Q2]), "operationType" : NewBodyOperationType.ADD, "oppositeDirection" : true, "depth" : 8 * mm});
        }
        {
            var Q0;
            Q0=makeQuery(id+"F9.boolean.opBoolean","MERGE",FACE,{"derivedFrom":[makeQuery(id+"F1.opExtrude","CAP_FACE",FACE,{"disambiguationData":[OSD([sQuery(id+"F0.wireOp",EDGE,"E0.bottom"),sQuery(id+"F0.wireOp",EDGE,"E0.top"),sQuery(id+"F0.wireOp",EDGE,"E0.left"),sQuery(id+"F0.wireOp",EDGE,"E0.right"),sQuery(id+"F0.wireOp",EDGE,"E3.0"),sQuery(id+"F0.wireOp",EDGE,"E3.1"),sQuery(id+"F0.wireOp",EDGE,"E3.2"),sQuery(id+"F0.wireOp",EDGE,"E3.3"),sQuery(id+"F0.wireOp",EDGE,"E4.filletArc"),sQuery(id+"F0.wireOp",EDGE,"E6.filletArc"),sQuery(id+"F0.wireOp",EDGE,"E9.filletArc"),sQuery(id+"F0.wireOp",EDGE,"E10.filletArc"),sQuery(id+"F0.wireOp",EDGE,"E12"),sQuery(id+"F0.wireOp",EDGE,"E13"),sQuery(id+"F0.wireOp",EDGE,"E14"),sQuery(id+"F0.wireOp",EDGE,"E15")])],"isStart":false}),makeQuery(id+"F9.opExtrude","CAP_FACE",FACE,{"disambiguationData":[OSD([sQuery(id+"F8.wireOp",EDGE,"E50.0"),sQuery(id+"F8.wireOp",EDGE,"E50.1"),sQuery(id+"F8.wireOp",EDGE,"E50.2"),sQuery(id+"F8.wireOp",EDGE,"E50.3"),sQuery(id+"F8.wireOp",EDGE,"E50.4"),sQuery(id+"F8.wireOp",EDGE,"E50.5"),sQuery(id+"F8.wireOp",EDGE,"E51.top"),sQuery(id+"F8.wireOp",EDGE,"E51.left"),sQuery(id+"F8.wireOp",EDGE,"E51.right"),sQuery(id+"F8.wireOp",EDGE,"E52.top"),sQuery(id+"F8.wireOp",EDGE,"E52.left"),sQuery(id+"F8.wireOp",EDGE,"E52.right"),sQuery(id+"F8.wireOp",EDGE,"E54.0"),sQuery(id+"F8.wireOp",EDGE,"E54.1"),sQuery(id+"F8.wireOp",EDGE,"E54.2"),sQuery(id+"F8.wireOp",EDGE,"E54.3"),sQuery(id+"F8.wireOp",EDGE,"E54.4"),sQuery(id+"F8.wireOp",EDGE,"E54.5")])],"isStart":true})]});
            var sketch = newSketch(context, id + "F10", { "sketchPlane" : qUnion([Q0])});
            skSolve(sketch);
        }
        {
            var Q0;
            Q0=makeQuery(id+"F10.imprint","IMPRINT",FACE,{"disambiguationData":[TD([[makeQuery(id+"F10.imprint","IMPRINT",EDGE,{"derivedFrom":makeQuery(id+"F9.opExtrude","CAP_EDGE",EDGE,{"disambiguationData":[OSD([sQuery(id+"F8.wireOp",EDGE,"E50.0")])],"isStart":true})}),-1.0]])]});
            extrude(context, id + "F11", {"entities" : qUnion([Q0]), "operationType" : NewBodyOperationType.ADD, "oppositeDirection" : true, "depth" : 1 * mm});
        }
        {
            var Q0;
            Q0=makeQuery(id+"F1.opExtrude","SWEPT_BODY",BODY,{"disambiguationData":[OSD([sQuery(id+"F0.wireOp",EDGE,"E0.bottom"),sQuery(id+"F0.wireOp",EDGE,"E0.top"),sQuery(id+"F0.wireOp",EDGE,"E0.left"),sQuery(id+"F0.wireOp",EDGE,"E0.right"),sQuery(id+"F0.wireOp",EDGE,"E3.0"),sQuery(id+"F0.wireOp",EDGE,"E3.1"),sQuery(id+"F0.wireOp",EDGE,"E3.2"),sQuery(id+"F0.wireOp",EDGE,"E3.3"),sQuery(id+"F0.wireOp",EDGE,"E4.filletArc"),sQuery(id+"F0.wireOp",EDGE,"E6.filletArc"),sQuery(id+"F0.wireOp",EDGE,"E9.filletArc"),sQuery(id+"F0.wireOp",EDGE,"E10.filletArc"),sQuery(id+"F0.wireOp",EDGE,"E12"),sQuery(id+"F0.wireOp",EDGE,"E13"),sQuery(id+"F0.wireOp",EDGE,"E14"),sQuery(id+"F0.wireOp",EDGE,"E15")])]});
            var Q1;
            {var subQ0=sQuery(id+"F8.wireOp",EDGE,"E50.5");var subQ1=sQuery(id+"F8.wireOp",EDGE,"E50.4");var subQ2=sQuery(id+"F8.wireOp",EDGE,"E50.3");var subQ3=sQuery(id+"F8.wireOp",EDGE,"E50.2");var subQ4=sQuery(id+"F8.wireOp",EDGE,"E50.1");var subQ5=sQuery(id+"F8.wireOp",EDGE,"E50.0");Q1=makeQuery(id+"F11.boolean.opBoolean","MERGE",FACE,{"derivedFrom":[makeQuery(id+"F9.boolean.opBoolean","MERGE",FACE,{"derivedFrom":[makeQuery(id+"F1.opExtrude","CAP_FACE",FACE,{"disambiguationData":[OSD([sQuery(id+"F0.wireOp",EDGE,"E0.bottom"),sQuery(id+"F0.wireOp",EDGE,"E0.top"),sQuery(id+"F0.wireOp",EDGE,"E0.left"),sQuery(id+"F0.wireOp",EDGE,"E0.right"),sQuery(id+"F0.wireOp",EDGE,"E3.0"),sQuery(id+"F0.wireOp",EDGE,"E3.1"),sQuery(id+"F0.wireOp",EDGE,"E3.2"),sQuery(id+"F0.wireOp",EDGE,"E3.3"),sQuery(id+"F0.wireOp",EDGE,"E4.filletArc"),sQuery(id+"F0.wireOp",EDGE,"E6.filletArc"),sQuery(id+"F0.wireOp",EDGE,"E9.filletArc"),sQuery(id+"F0.wireOp",EDGE,"E10.filletArc"),sQuery(id+"F0.wireOp",EDGE,"E12"),sQuery(id+"F0.wireOp",EDGE,"E13"),sQuery(id+"F0.wireOp",EDGE,"E14"),sQuery(id+"F0.wireOp",EDGE,"E15")])],"isStart":false}),makeQuery(id+"F9.opExtrude","CAP_FACE",FACE,{"disambiguationData":[OSD([subQ5,subQ4,subQ3,subQ2,subQ1,subQ0,sQuery(id+"F8.wireOp",EDGE,"E51.top"),sQuery(id+"F8.wireOp",EDGE,"E51.left"),sQuery(id+"F8.wireOp",EDGE,"E51.right"),sQuery(id+"F8.wireOp",EDGE,"E52.top"),sQuery(id+"F8.wireOp",EDGE,"E52.left"),sQuery(id+"F8.wireOp",EDGE,"E52.right"),sQuery(id+"F8.wireOp",EDGE,"E54.0"),sQuery(id+"F8.wireOp",EDGE,"E54.1"),sQuery(id+"F8.wireOp",EDGE,"E54.2"),sQuery(id+"F8.wireOp",EDGE,"E54.3"),sQuery(id+"F8.wireOp",EDGE,"E54.4"),sQuery(id+"F8.wireOp",EDGE,"E54.5")])],"isStart":true})]}),makeQuery(id+"F11.opExtrude","CAP_FACE",FACE,{"disambiguationData":[OSD([subQ5,subQ4,subQ3,subQ2,subQ1,subQ0])],"isStart":true})]});}
            mirror(context, id + "F12", {"entities" : qUnion([Q0]), "mirrorPlane" : qUnion([Q1])});
        }
        {
            var Q0;
            Q0=makeQuery(id+"F12.opPattern","COPY",FACE,{"derivedFrom":makeQuery(id+"F1.opExtrude","CAP_FACE",FACE,{"disambiguationData":[OSD([sQuery(id+"F0.wireOp",EDGE,"E0.bottom"),sQuery(id+"F0.wireOp",EDGE,"E0.top"),sQuery(id+"F0.wireOp",EDGE,"E0.left"),sQuery(id+"F0.wireOp",EDGE,"E0.right"),sQuery(id+"F0.wireOp",EDGE,"E3.0"),sQuery(id+"F0.wireOp",EDGE,"E3.1"),sQuery(id+"F0.wireOp",EDGE,"E3.2"),sQuery(id+"F0.wireOp",EDGE,"E3.3"),sQuery(id+"F0.wireOp",EDGE,"E4.filletArc"),sQuery(id+"F0.wireOp",EDGE,"E6.filletArc"),sQuery(id+"F0.wireOp",EDGE,"E9.filletArc"),sQuery(id+"F0.wireOp",EDGE,"E10.filletArc"),sQuery(id+"F0.wireOp",EDGE,"E12"),sQuery(id+"F0.wireOp",EDGE,"E13"),sQuery(id+"F0.wireOp",EDGE,"E14"),sQuery(id+"F0.wireOp",EDGE,"E15")])],"isStart":true}),"instanceName":"1"});
            var sketch = newSketch(context, id + "F13", { "sketchPlane" : qUnion([Q0])});
            skSolve(sketch);
        }
        {
            var Q0;
            Q0=makeQuery(id+"F13.imprint","IMPRINT",FACE,{"disambiguationData":[TD([[makeQuery(id+"F13.imprint","IMPRINT",EDGE,{"derivedFrom":makeQuery(id+"F12.opPattern","COPY",EDGE,{"derivedFrom":makeQuery(id+"F1.opExtrude","CAP_EDGE",EDGE,{"disambiguationData":[OSD([sQuery(id+"F0.wireOp",EDGE,"E0.bottom")])],"isStart":true}),"instanceName":"1"})}),-1.0]])]});
            var Q1;
            {var subQ15=sQuery(id+"F0.wireOp",EDGE,"E0.bottom");Q1=makeQuery(id+"F13.imprint","IMPRINT",FACE,{"disambiguationData":[TD([[makeQuery(id+"F13.imprint","IMPRINT",EDGE,{"derivedFrom":makeQuery(id+"F12.opPattern","COPY",EDGE,{"derivedFrom":makeQuery(id+"F1.opExtrude","CAP_EDGE",EDGE,{"disambiguationData":[OSD([subQ15])],"isStart":true}),"instanceName":"1"})}),1.0]])]});}
            extrude(context, id + "F14", {"entities" : qUnion([Q0, Q1]), "depth" : 5.7 * mm});
        }
        {
            var Q0;
            Q0=makeQuery(id+"F14.opExtrude","CAP_FACE",FACE,{"disambiguationData":[OSD([sQuery(id+"F0.wireOp",EDGE,"E0.bottom"),sQuery(id+"F0.wireOp",EDGE,"E0.top"),sQuery(id+"F0.wireOp",EDGE,"E0.left"),sQuery(id+"F0.wireOp",EDGE,"E0.right"),sQuery(id+"F0.wireOp",EDGE,"E3.0"),sQuery(id+"F0.wireOp",EDGE,"E3.1"),sQuery(id+"F0.wireOp",EDGE,"E3.2"),sQuery(id+"F0.wireOp",EDGE,"E3.3"),sQuery(id+"F0.wireOp",EDGE,"E4.filletArc"),sQuery(id+"F0.wireOp",EDGE,"E6.filletArc"),sQuery(id+"F0.wireOp",EDGE,"E9.filletArc"),sQuery(id+"F0.wireOp",EDGE,"E10.filletArc"),sQuery(id+"F0.wireOp",EDGE,"E12"),sQuery(id+"F0.wireOp",EDGE,"E13"),sQuery(id+"F0.wireOp",EDGE,"E14"),sQuery(id+"F0.wireOp",EDGE,"E15"),sQuery(id+"F6.wireOp",EDGE,"E46.0"),sQuery(id+"F6.wireOp",EDGE,"E46.1"),sQuery(id+"F6.wireOp",EDGE,"E46.2"),sQuery(id+"F6.wireOp",EDGE,"E46.3"),sQuery(id+"F6.wireOp",EDGE,"E46.4"),sQuery(id+"F6.wireOp",EDGE,"E46.5"),sQuery(id+"F6.wireOp",EDGE,"E47.0"),sQuery(id+"F6.wireOp",EDGE,"E47.1"),sQuery(id+"F6.wireOp",EDGE,"E47.2"),sQuery(id+"F6.wireOp",EDGE,"E47.3"),sQuery(id+"F6.wireOp",EDGE,"E47.4"),sQuery(id+"F6.wireOp",EDGE,"E47.5"),sQuery(id+"F6.wireOp",EDGE,"E48.0"),sQuery(id+"F6.wireOp",EDGE,"E48.1"),sQuery(id+"F6.wireOp",EDGE,"E48.2"),sQuery(id+"F6.wireOp",EDGE,"E48.3"),sQuery(id+"F6.wireOp",EDGE,"E48.4"),sQuery(id+"F6.wireOp",EDGE,"E48.5"),sQuery(id+"F6.wireOp",EDGE,"E49.0"),sQuery(id+"F6.wireOp",EDGE,"E49.1"),sQuery(id+"F6.wireOp",EDGE,"E49.2"),sQuery(id+"F6.wireOp",EDGE,"E49.3"),sQuery(id+"F6.wireOp",EDGE,"E49.4"),sQuery(id+"F6.wireOp",EDGE,"E49.5")])],"isStart":true});
            var sketch = newSketch(context, id + "F15", { "sketchPlane" : qUnion([Q0])});
            skLineSegment(sketch, "E55.0.0", {"start": v(-24.1, -10.95) * mm, "end": v(-30.42, 0) * mm});
            skLineSegment(sketch, "E55.0.1", {"start": v(-30.42, 0) * mm, "end": v(-24.1, 10.95) * mm});
            skLineSegment(sketch, "E55.0.2", {"start": v(-24.1, 10.95) * mm, "end": v(-11.46, 10.95) * mm});
            skLineSegment(sketch, "E55.0.3", {"start": v(-11.46, 10.95) * mm, "end": v(-5.14, 0) * mm});
            skLineSegment(sketch, "E55.0.4", {"start": v(-5.14, 0) * mm, "end": v(-11.46, -10.95) * mm});
            skLineSegment(sketch, "E55.0.5", {"start": v(-11.46, -10.95) * mm, "end": v(-24.1, -10.95) * mm});
            skLineSegment(sketch, "E55.1.0", {"start": v(11.17, -10.95) * mm, "end": v(4.85, 0) * mm});
            skLineSegment(sketch, "E55.1.1", {"start": v(4.85, 0) * mm, "end": v(11.17, 10.95) * mm});
            skLineSegment(sketch, "E55.1.2", {"start": v(11.17, 10.95) * mm, "end": v(23.82, 10.95) * mm});
            skLineSegment(sketch, "E55.1.3", {"start": v(23.82, 10.95) * mm, "end": v(30.14, 0) * mm});
            skLineSegment(sketch, "E55.1.4", {"start": v(30.14, 0) * mm, "end": v(23.82, -10.95) * mm});
            skLineSegment(sketch, "E55.1.5", {"start": v(23.82, -10.95) * mm, "end": v(11.17, -10.95) * mm});
            skLineSegment(sketch, "E56.1.0", {"start": v(-15.33, -4.25) * mm, "end": v(-20.23, -4.25) * mm});
            skLineSegment(sketch, "E56.1.1", {"start": v(-20.23, -4.25) * mm, "end": v(-22.69, 0) * mm});
            skLineSegment(sketch, "E56.1.2", {"start": v(-22.69, 0) * mm, "end": v(-20.23, 4.25) * mm});
            skLineSegment(sketch, "E56.1.3", {"start": v(-20.23, 4.25) * mm, "end": v(-15.33, 4.25) * mm});
            skLineSegment(sketch, "E56.1.4", {"start": v(-15.33, 4.25) * mm, "end": v(-12.87, 0) * mm});
            skLineSegment(sketch, "E56.1.5", {"start": v(-12.87, 0) * mm, "end": v(-15.33, -4.25) * mm});
            skSolve(sketch);
        }
        {
            var Q0;
            Q0=makeQuery(id+"F15.imprint","IMPRINT",FACE,{"disambiguationData":[TD([[makeQuery(id+"F15.imprint","IMPRINT",EDGE,{"derivedFrom":sQuery(id+"F15.wireOp",EDGE,"E55.0.0")}),-1.0]])]});
            var Q1;
            Q1=makeQuery(id+"F15.imprint","IMPRINT",FACE,{"disambiguationData":[TD([[makeQuery(id+"F15.imprint","IMPRINT",EDGE,{"derivedFrom":sQuery(id+"F15.wireOp",EDGE,"E55.1.0")}),-1.0]])]});
            extrude(context, id + "F16", {"entities" : qUnion([Q0, Q1]), "operationType" : NewBodyOperationType.REMOVE, "oppositeDirection" : true, "depth" : 5 * mm});
        }
        {
            var Q0;
            Q0=makeQuery(id+"F16.boolean.opBoolean","SPLIT",FACE,{"disambiguationData":[TD([makeQuery(id+"F16.opExtrude","SWEPT_FACE",FACE,{"disambiguationData":[OSD([sQuery(id+"F15.wireOp",EDGE,"E56.0.0")])]})])],"derivedFrom":makeQuery(id+"F14.opExtrude","CAP_FACE",FACE,{"disambiguationData":[OSD([sQuery(id+"F0.wireOp",EDGE,"E0.bottom"),sQuery(id+"F0.wireOp",EDGE,"E0.top"),sQuery(id+"F0.wireOp",EDGE,"E0.left"),sQuery(id+"F0.wireOp",EDGE,"E0.right"),sQuery(id+"F0.wireOp",EDGE,"E3.0"),sQuery(id+"F0.wireOp",EDGE,"E3.1"),sQuery(id+"F0.wireOp",EDGE,"E3.2"),sQuery(id+"F0.wireOp",EDGE,"E3.3"),sQuery(id+"F0.wireOp",EDGE,"E4.filletArc"),sQuery(id+"F0.wireOp",EDGE,"E6.filletArc"),sQuery(id+"F0.wireOp",EDGE,"E9.filletArc"),sQuery(id+"F0.wireOp",EDGE,"E10.filletArc"),sQuery(id+"F0.wireOp",EDGE,"E12"),sQuery(id+"F0.wireOp",EDGE,"E13"),sQuery(id+"F0.wireOp",EDGE,"E14"),sQuery(id+"F0.wireOp",EDGE,"E15"),sQuery(id+"F6.wireOp",EDGE,"E46.0"),sQuery(id+"F6.wireOp",EDGE,"E46.1"),sQuery(id+"F6.wireOp",EDGE,"E46.2"),sQuery(id+"F6.wireOp",EDGE,"E46.3"),sQuery(id+"F6.wireOp",EDGE,"E46.4"),sQuery(id+"F6.wireOp",EDGE,"E46.5"),sQuery(id+"F6.wireOp",EDGE,"E47.0"),sQuery(id+"F6.wireOp",EDGE,"E47.1"),sQuery(id+"F6.wireOp",EDGE,"E47.2"),sQuery(id+"F6.wireOp",EDGE,"E47.3"),sQuery(id+"F6.wireOp",EDGE,"E47.4"),sQuery(id+"F6.wireOp",EDGE,"E47.5"),sQuery(id+"F6.wireOp",EDGE,"E48.0"),sQuery(id+"F6.wireOp",EDGE,"E48.1"),sQuery(id+"F6.wireOp",EDGE,"E48.2"),sQuery(id+"F6.wireOp",EDGE,"E48.3"),sQuery(id+"F6.wireOp",EDGE,"E48.4"),sQuery(id+"F6.wireOp",EDGE,"E48.5"),sQuery(id+"F6.wireOp",EDGE,"E49.0"),sQuery(id+"F6.wireOp",EDGE,"E49.1"),sQuery(id+"F6.wireOp",EDGE,"E49.2"),sQuery(id+"F6.wireOp",EDGE,"E49.3"),sQuery(id+"F6.wireOp",EDGE,"E49.4"),sQuery(id+"F6.wireOp",EDGE,"E49.5")])],"isStart":true})});
            var Q1;
            Q1=makeQuery(id+"F16.boolean.opBoolean","SPLIT",FACE,{"disambiguationData":[TD([makeQuery(id+"F16.opExtrude","SWEPT_FACE",FACE,{"disambiguationData":[OSD([sQuery(id+"F15.wireOp",EDGE,"E56.1.0")])]})])],"derivedFrom":makeQuery(id+"F14.opExtrude","CAP_FACE",FACE,{"disambiguationData":[OSD([sQuery(id+"F0.wireOp",EDGE,"E0.bottom"),sQuery(id+"F0.wireOp",EDGE,"E0.top"),sQuery(id+"F0.wireOp",EDGE,"E0.left"),sQuery(id+"F0.wireOp",EDGE,"E0.right"),sQuery(id+"F0.wireOp",EDGE,"E3.0"),sQuery(id+"F0.wireOp",EDGE,"E3.1"),sQuery(id+"F0.wireOp",EDGE,"E3.2"),sQuery(id+"F0.wireOp",EDGE,"E3.3"),sQuery(id+"F0.wireOp",EDGE,"E4.filletArc"),sQuery(id+"F0.wireOp",EDGE,"E6.filletArc"),sQuery(id+"F0.wireOp",EDGE,"E9.filletArc"),sQuery(id+"F0.wireOp",EDGE,"E10.filletArc"),sQuery(id+"F0.wireOp",EDGE,"E12"),sQuery(id+"F0.wireOp",EDGE,"E13"),sQuery(id+"F0.wireOp",EDGE,"E14"),sQuery(id+"F0.wireOp",EDGE,"E15"),sQuery(id+"F6.wireOp",EDGE,"E46.0"),sQuery(id+"F6.wireOp",EDGE,"E46.1"),sQuery(id+"F6.wireOp",EDGE,"E46.2"),sQuery(id+"F6.wireOp",EDGE,"E46.3"),sQuery(id+"F6.wireOp",EDGE,"E46.4"),sQuery(id+"F6.wireOp",EDGE,"E46.5"),sQuery(id+"F6.wireOp",EDGE,"E47.0"),sQuery(id+"F6.wireOp",EDGE,"E47.1"),sQuery(id+"F6.wireOp",EDGE,"E47.2"),sQuery(id+"F6.wireOp",EDGE,"E47.3"),sQuery(id+"F6.wireOp",EDGE,"E47.4"),sQuery(id+"F6.wireOp",EDGE,"E47.5"),sQuery(id+"F6.wireOp",EDGE,"E48.0"),sQuery(id+"F6.wireOp",EDGE,"E48.1"),sQuery(id+"F6.wireOp",EDGE,"E48.2"),sQuery(id+"F6.wireOp",EDGE,"E48.3"),sQuery(id+"F6.wireOp",EDGE,"E48.4"),sQuery(id+"F6.wireOp",EDGE,"E48.5"),sQuery(id+"F6.wireOp",EDGE,"E49.0"),sQuery(id+"F6.wireOp",EDGE,"E49.1"),sQuery(id+"F6.wireOp",EDGE,"E49.2"),sQuery(id+"F6.wireOp",EDGE,"E49.3"),sQuery(id+"F6.wireOp",EDGE,"E49.4"),sQuery(id+"F6.wireOp",EDGE,"E49.5")])],"isStart":true})});
            extrude(context, id + "F17", {"entities" : qUnion([Q0, Q1]), "operationType" : NewBodyOperationType.REMOVE, "endBound" : BoundingType.THROUGH_ALL, "oppositeDirection" : true, "depth" : 25.4 * mm});
        }
        {
            var Q0;
            {var subQ0=sQuery(id+"F6.wireOp",EDGE,"E48.0");var subQ1=sQuery(id+"F0.wireOp",EDGE,"E15");var subQ2=sQuery(id+"F0.wireOp",EDGE,"E14");var subQ3=sQuery(id+"F0.wireOp",EDGE,"E13");var subQ4=sQuery(id+"F0.wireOp",EDGE,"E12");var subQ5=sQuery(id+"F0.wireOp",EDGE,"E10.filletArc");var subQ6=sQuery(id+"F0.wireOp",EDGE,"E9.filletArc");var subQ7=sQuery(id+"F0.wireOp",EDGE,"E6.filletArc");var subQ8=sQuery(id+"F0.wireOp",EDGE,"E4.filletArc");var subQ9=sQuery(id+"F0.wireOp",EDGE,"E3.3");var subQ10=sQuery(id+"F0.wireOp",EDGE,"E3.2");var subQ11=sQuery(id+"F0.wireOp",EDGE,"E3.1");var subQ12=sQuery(id+"F0.wireOp",EDGE,"E3.0");var subQ13=sQuery(id+"F0.wireOp",EDGE,"E0.right");var subQ14=sQuery(id+"F0.wireOp",EDGE,"E0.left");var subQ15=sQuery(id+"F0.wireOp",EDGE,"E0.top");var subQ16=sQuery(id+"F0.wireOp",EDGE,"E0.bottom");var subQ17=sQuery(id+"F6.wireOp",EDGE,"E47.5");var subQ18=sQuery(id+"F6.wireOp",EDGE,"E47.4");var subQ19=sQuery(id+"F6.wireOp",EDGE,"E47.3");var subQ20=sQuery(id+"F6.wireOp",EDGE,"E47.2");var subQ21=sQuery(id+"F6.wireOp",EDGE,"E47.1");var subQ22=sQuery(id+"F6.wireOp",EDGE,"E47.0");var subQ23=sQuery(id+"F6.wireOp",EDGE,"E46.5");var subQ24=sQuery(id+"F6.wireOp",EDGE,"E46.4");var subQ25=sQuery(id+"F6.wireOp",EDGE,"E46.3");var subQ26=sQuery(id+"F6.wireOp",EDGE,"E46.2");var subQ27=sQuery(id+"F6.wireOp",EDGE,"E48.1");var subQ28=sQuery(id+"F6.wireOp",EDGE,"E46.1");var subQ29=sQuery(id+"F6.wireOp",EDGE,"E46.0");var subQ30=sQuery(id+"F6.wireOp",EDGE,"E48.2");var subQ31=sQuery(id+"F6.wireOp",EDGE,"E48.3");var subQ32=sQuery(id+"F6.wireOp",EDGE,"E48.4");var subQ33=sQuery(id+"F6.wireOp",EDGE,"E48.5");var subQ34=sQuery(id+"F6.wireOp",EDGE,"E49.0");var subQ35=sQuery(id+"F6.wireOp",EDGE,"E49.1");var subQ36=sQuery(id+"F6.wireOp",EDGE,"E49.2");var subQ37=sQuery(id+"F6.wireOp",EDGE,"E49.3");var subQ38=sQuery(id+"F6.wireOp",EDGE,"E49.4");var subQ39=sQuery(id+"F6.wireOp",EDGE,"E49.5");Q0=makeQuery(id+"F16.boolean.opBoolean","SPLIT",FACE,{"disambiguationData":[TD([makeQuery(id+"F14.opExtrude","SWEPT_FACE",FACE,{"disambiguationData":[OSD([subQ12])]})])],"derivedFrom":makeQuery(id+"F14.opExtrude","CAP_FACE",FACE,{"disambiguationData":[OSD([subQ16,subQ15,subQ14,subQ13,subQ12,subQ11,subQ10,subQ9,subQ8,subQ7,subQ6,subQ5,subQ4,subQ3,subQ2,subQ1,subQ29,subQ28,subQ26,subQ25,subQ24,subQ23,subQ22,subQ21,subQ20,subQ19,subQ18,subQ17,subQ0,subQ27,subQ30,subQ31,subQ32,subQ33,subQ34,subQ35,subQ36,subQ37,subQ38,subQ39])],"isStart":true})});}
            var sketch = newSketch(context, id + "F18", { "sketchPlane" : qUnion([Q0])});
            skCircle(sketch, "E57.cCircle", {"center": v(-20.33, 34.25) * mm, "radius": 2.16 * mm, "construction": true});
            skLineSegment(sketch, "E57.0", {"start": v(-21.57, 36.41) * mm, "end": v(-19.08, 36.41) * mm});
            skLineSegment(sketch, "E57.1", {"start": v(-19.08, 36.41) * mm, "end": v(-17.83, 34.25) * mm});
            skLineSegment(sketch, "E57.2", {"start": v(-17.83, 34.25) * mm, "end": v(-19.08, 32.1) * mm});
            skLineSegment(sketch, "E57.3", {"start": v(-19.08, 32.1) * mm, "end": v(-21.57, 32.1) * mm});
            skLineSegment(sketch, "E57.4", {"start": v(-21.57, 32.1) * mm, "end": v(-22.82, 34.25) * mm});
            skLineSegment(sketch, "E57.5", {"start": v(-22.82, 34.25) * mm, "end": v(-21.57, 36.41) * mm});
            skPoint(sketch, "E57.0.midPoint", {"position": v(-20.33, 36.41) * mm});
            skCircle(sketch, "E58.cCircle", {"center": v(22.76, 34.25) * mm, "radius": 2.16 * mm, "construction": true});
            skLineSegment(sketch, "E58.0", {"start": v(21.51, 36.41) * mm, "end": v(24, 36.41) * mm});
            skLineSegment(sketch, "E58.1", {"start": v(24, 36.41) * mm, "end": v(25.25, 34.25) * mm});
            skLineSegment(sketch, "E58.2", {"start": v(25.25, 34.25) * mm, "end": v(24, 32.1) * mm});
            skLineSegment(sketch, "E58.3", {"start": v(24, 32.1) * mm, "end": v(21.51, 32.1) * mm});
            skLineSegment(sketch, "E58.4", {"start": v(21.51, 32.1) * mm, "end": v(20.27, 34.25) * mm});
            skLineSegment(sketch, "E58.5", {"start": v(20.27, 34.25) * mm, "end": v(21.51, 36.41) * mm});
            skPoint(sketch, "E58.0.midPoint", {"position": v(22.76, 36.41) * mm});
            skCircle(sketch, "E59.cCircle", {"center": v(-20.33, -34.25) * mm, "radius": 2.16 * mm, "construction": true});
            skLineSegment(sketch, "E59.0", {"start": v(-21.57, -32.1) * mm, "end": v(-19.08, -32.1) * mm});
            skLineSegment(sketch, "E59.1", {"start": v(-19.08, -32.1) * mm, "end": v(-17.83, -34.25) * mm});
            skLineSegment(sketch, "E59.2", {"start": v(-17.83, -34.25) * mm, "end": v(-19.08, -36.41) * mm});
            skLineSegment(sketch, "E59.3", {"start": v(-19.08, -36.41) * mm, "end": v(-21.57, -36.41) * mm});
            skLineSegment(sketch, "E59.4", {"start": v(-21.57, -36.41) * mm, "end": v(-22.82, -34.25) * mm});
            skLineSegment(sketch, "E59.5", {"start": v(-22.82, -34.25) * mm, "end": v(-21.57, -32.1) * mm});
            skPoint(sketch, "E59.0.midPoint", {"position": v(-20.33, -32.1) * mm});
            skCircle(sketch, "E60.cCircle", {"center": v(22.76, -34.25) * mm, "radius": 2.16 * mm, "construction": true});
            skLineSegment(sketch, "E60.0", {"start": v(21.51, -32.1) * mm, "end": v(24, -32.1) * mm});
            skLineSegment(sketch, "E60.1", {"start": v(24, -32.1) * mm, "end": v(25.25, -34.25) * mm});
            skLineSegment(sketch, "E60.2", {"start": v(25.25, -34.25) * mm, "end": v(24, -36.41) * mm});
            skLineSegment(sketch, "E60.3", {"start": v(24, -36.41) * mm, "end": v(21.51, -36.41) * mm});
            skLineSegment(sketch, "E60.4", {"start": v(21.51, -36.41) * mm, "end": v(20.27, -34.25) * mm});
            skLineSegment(sketch, "E60.5", {"start": v(20.27, -34.25) * mm, "end": v(21.51, -32.1) * mm});
            skPoint(sketch, "E60.0.midPoint", {"position": v(22.76, -32.1) * mm});
            skCircle(sketch, "E61.cCircle", {"center": v(-53.3, 0) * mm, "radius": 2.16 * mm, "construction": true});
            skPoint(sketch, "E61.cCircle.centerSnap0", {"position": v(-53.3, 32.1) * mm});
            skLineSegment(sketch, "E61.0", {"start": v(-54.55, 2.16) * mm, "end": v(-52.06, 2.16) * mm});
            skLineSegment(sketch, "E61.1", {"start": v(-52.06, 2.16) * mm, "end": v(-50.8, 0) * mm});
            skLineSegment(sketch, "E61.2", {"start": v(-50.8, 0) * mm, "end": v(-52.06, -2.16) * mm});
            skLineSegment(sketch, "E61.3", {"start": v(-52.06, -2.16) * mm, "end": v(-54.55, -2.16) * mm});
            skLineSegment(sketch, "E61.4", {"start": v(-54.55, -2.16) * mm, "end": v(-55.8, 0) * mm});
            skLineSegment(sketch, "E61.5", {"start": v(-55.8, 0) * mm, "end": v(-54.55, 2.16) * mm});
            skPoint(sketch, "E61.0.midPoint", {"position": v(-53.3, 2.16) * mm});
            skCircle(sketch, "E62.cCircle", {"center": v(22.76, 34.25) * mm, "radius": 4.06 * mm, "construction": true});
            skLineSegment(sketch, "E62.0", {"start": v(25.1, 30.19) * mm, "end": v(20.41, 30.19) * mm});
            skLineSegment(sketch, "E62.1", {"start": v(20.41, 30.19) * mm, "end": v(18.07, 34.25) * mm});
            skLineSegment(sketch, "E62.2", {"start": v(18.07, 34.25) * mm, "end": v(20.41, 38.32) * mm});
            skLineSegment(sketch, "E62.3", {"start": v(20.41, 38.32) * mm, "end": v(25.1, 38.32) * mm});
            skLineSegment(sketch, "E62.4", {"start": v(25.1, 38.32) * mm, "end": v(27.45, 34.25) * mm});
            skLineSegment(sketch, "E62.5", {"start": v(27.45, 34.25) * mm, "end": v(25.1, 30.19) * mm});
            skPoint(sketch, "E62.0.midPoint", {"position": v(22.76, 30.19) * mm});
            skCircle(sketch, "E63.cCircle", {"center": v(-20.33, 34.25) * mm, "radius": 4.06 * mm, "construction": true});
            skLineSegment(sketch, "E63.0", {"start": v(-17.98, 30.19) * mm, "end": v(-22.67, 30.19) * mm});
            skLineSegment(sketch, "E63.1", {"start": v(-22.67, 30.19) * mm, "end": v(-25.02, 34.25) * mm});
            skLineSegment(sketch, "E63.2", {"start": v(-25.02, 34.25) * mm, "end": v(-22.67, 38.32) * mm});
            skLineSegment(sketch, "E63.3", {"start": v(-22.67, 38.32) * mm, "end": v(-17.98, 38.32) * mm});
            skLineSegment(sketch, "E63.4", {"start": v(-17.98, 38.32) * mm, "end": v(-15.63, 34.25) * mm});
            skLineSegment(sketch, "E63.5", {"start": v(-15.63, 34.25) * mm, "end": v(-17.98, 30.19) * mm});
            skPoint(sketch, "E63.0.midPoint", {"position": v(-20.33, 30.19) * mm});
            skCircle(sketch, "E64.cCircle", {"center": v(-53.3, 0) * mm, "radius": 4.06 * mm, "construction": true});
            skLineSegment(sketch, "E64.0", {"start": v(-55.65, 4.06) * mm, "end": v(-50.96, 4.06) * mm});
            skLineSegment(sketch, "E64.1", {"start": v(-50.96, 4.06) * mm, "end": v(-48.6, 0) * mm});
            skLineSegment(sketch, "E64.2", {"start": v(-48.6, 0) * mm, "end": v(-50.96, -4.06) * mm});
            skLineSegment(sketch, "E64.3", {"start": v(-50.96, -4.06) * mm, "end": v(-55.65, -4.06) * mm});
            skLineSegment(sketch, "E64.4", {"start": v(-55.65, -4.06) * mm, "end": v(-58, 0) * mm});
            skLineSegment(sketch, "E64.5", {"start": v(-58, 0) * mm, "end": v(-55.65, 4.06) * mm});
            skPoint(sketch, "E64.0.midPoint", {"position": v(-53.3, 4.06) * mm});
            skCircle(sketch, "E65.cCircle", {"center": v(-20.33, -34.25) * mm, "radius": 4.06 * mm, "construction": true});
            skLineSegment(sketch, "E65.0", {"start": v(-22.67, -30.19) * mm, "end": v(-17.98, -30.19) * mm});
            skLineSegment(sketch, "E65.1", {"start": v(-17.98, -30.19) * mm, "end": v(-15.63, -34.25) * mm});
            skLineSegment(sketch, "E65.2", {"start": v(-15.63, -34.25) * mm, "end": v(-17.98, -38.32) * mm});
            skLineSegment(sketch, "E65.3", {"start": v(-17.98, -38.32) * mm, "end": v(-22.67, -38.32) * mm});
            skLineSegment(sketch, "E65.4", {"start": v(-22.67, -38.32) * mm, "end": v(-25.02, -34.25) * mm});
            skLineSegment(sketch, "E65.5", {"start": v(-25.02, -34.25) * mm, "end": v(-22.67, -30.19) * mm});
            skPoint(sketch, "E65.0.midPoint", {"position": v(-20.33, -30.19) * mm});
            skCircle(sketch, "E66.cCircle", {"center": v(22.76, -34.25) * mm, "radius": 4.06 * mm, "construction": true});
            skLineSegment(sketch, "E66.0", {"start": v(20.41, -30.19) * mm, "end": v(25.1, -30.19) * mm});
            skLineSegment(sketch, "E66.1", {"start": v(25.1, -30.19) * mm, "end": v(27.45, -34.25) * mm});
            skLineSegment(sketch, "E66.2", {"start": v(27.45, -34.25) * mm, "end": v(25.1, -38.32) * mm});
            skLineSegment(sketch, "E66.3", {"start": v(25.1, -38.32) * mm, "end": v(20.41, -38.32) * mm});
            skLineSegment(sketch, "E66.4", {"start": v(20.41, -38.32) * mm, "end": v(18.07, -34.25) * mm});
            skLineSegment(sketch, "E66.5", {"start": v(18.07, -34.25) * mm, "end": v(20.41, -30.19) * mm});
            skPoint(sketch, "E66.0.midPoint", {"position": v(22.76, -30.19) * mm});
            skCircle(sketch, "E67.cCircle", {"center": v(53.3, 0) * mm, "radius": 2.16 * mm, "construction": true});
            skLineSegment(sketch, "E67.0", {"start": v(52.06, 2.16) * mm, "end": v(54.55, 2.16) * mm});
            skLineSegment(sketch, "E67.1", {"start": v(54.55, 2.16) * mm, "end": v(55.8, 0) * mm});
            skLineSegment(sketch, "E67.2", {"start": v(55.8, 0) * mm, "end": v(54.55, -2.16) * mm});
            skLineSegment(sketch, "E67.3", {"start": v(54.55, -2.16) * mm, "end": v(52.06, -2.16) * mm});
            skLineSegment(sketch, "E67.4", {"start": v(52.06, -2.16) * mm, "end": v(50.8, 0) * mm});
            skLineSegment(sketch, "E67.5", {"start": v(50.8, 0) * mm, "end": v(52.06, 2.16) * mm});
            skPoint(sketch, "E67.0.midPoint", {"position": v(53.3, 2.16) * mm});
            skCircle(sketch, "E68.cCircle", {"center": v(53.3, 0) * mm, "radius": 4.06 * mm, "construction": true});
            skLineSegment(sketch, "E68.0", {"start": v(50.96, 4.06) * mm, "end": v(55.65, 4.06) * mm});
            skLineSegment(sketch, "E68.1", {"start": v(55.65, 4.06) * mm, "end": v(58, 0) * mm});
            skLineSegment(sketch, "E68.2", {"start": v(58, 0) * mm, "end": v(55.65, -4.06) * mm});
            skLineSegment(sketch, "E68.3", {"start": v(55.65, -4.06) * mm, "end": v(50.96, -4.06) * mm});
            skLineSegment(sketch, "E68.4", {"start": v(50.96, -4.06) * mm, "end": v(48.6, 0) * mm});
            skLineSegment(sketch, "E68.5", {"start": v(48.6, 0) * mm, "end": v(50.96, 4.06) * mm});
            skPoint(sketch, "E68.0.midPoint", {"position": v(53.3, 4.06) * mm});
            skSolve(sketch);
        }
        {
            var Q0;
            Q0=makeQuery(id+"F18.imprint","IMPRINT",FACE,{"disambiguationData":[TD([[makeQuery(id+"F18.imprint","IMPRINT",EDGE,{"derivedFrom":sQuery(id+"F18.wireOp",EDGE,"E61.0")}),-1.0]])]});
            var Q1;
            Q1=makeQuery(id+"F18.imprint","IMPRINT",FACE,{"disambiguationData":[TD([[makeQuery(id+"F18.imprint","IMPRINT",EDGE,{"derivedFrom":sQuery(id+"F18.wireOp",EDGE,"E59.0")}),-1.0]])]});
            var Q2;
            Q2=makeQuery(id+"F18.imprint","IMPRINT",FACE,{"disambiguationData":[TD([[makeQuery(id+"F18.imprint","IMPRINT",EDGE,{"derivedFrom":sQuery(id+"F18.wireOp",EDGE,"E60.0")}),-1.0]])]});
            var Q3;
            Q3=makeQuery(id+"F18.imprint","IMPRINT",FACE,{"disambiguationData":[TD([[makeQuery(id+"F18.imprint","IMPRINT",EDGE,{"derivedFrom":sQuery(id+"F18.wireOp",EDGE,"E57.0")}),-1.0]])]});
            var Q4;
            Q4=makeQuery(id+"F18.imprint","IMPRINT",FACE,{"disambiguationData":[TD([[makeQuery(id+"F18.imprint","IMPRINT",EDGE,{"derivedFrom":sQuery(id+"F18.wireOp",EDGE,"E58.0")}),-1.0]])]});
            var Q5;
            Q5=makeQuery(id+"F18.imprint","IMPRINT",FACE,{"disambiguationData":[TD([[makeQuery(id+"F18.imprint","IMPRINT",EDGE,{"derivedFrom":sQuery(id+"F18.wireOp",EDGE,"E67.0")}),-1.0]])]});
            extrude(context, id + "F19", {"entities" : qUnion([Q0, Q1, Q2, Q3, Q4, Q5]), "operationType" : NewBodyOperationType.REMOVE, "endBound" : BoundingType.THROUGH_ALL, "oppositeDirection" : true, "depth" : 25.4 * mm});
        }
        {
            var Q0;
            Q0=makeQuery(id+"F18.imprint","IMPRINT",FACE,{"disambiguationData":[TD([[makeQuery(id+"F18.imprint","IMPRINT",EDGE,{"derivedFrom":sQuery(id+"F18.wireOp",EDGE,"E61.0")}),1.0]])]});
            var Q1;
            Q1=makeQuery(id+"F18.imprint","IMPRINT",FACE,{"disambiguationData":[TD([[makeQuery(id+"F18.imprint","IMPRINT",EDGE,{"derivedFrom":sQuery(id+"F18.wireOp",EDGE,"E59.0")}),1.0]])]});
            var Q2;
            Q2=makeQuery(id+"F18.imprint","IMPRINT",FACE,{"disambiguationData":[TD([[makeQuery(id+"F18.imprint","IMPRINT",EDGE,{"derivedFrom":sQuery(id+"F18.wireOp",EDGE,"E60.0")}),1.0]])]});
            var Q3;
            Q3=makeQuery(id+"F18.imprint","IMPRINT",FACE,{"disambiguationData":[TD([[makeQuery(id+"F18.imprint","IMPRINT",EDGE,{"derivedFrom":sQuery(id+"F18.wireOp",EDGE,"E57.0")}),1.0]])]});
            var Q4;
            Q4=makeQuery(id+"F18.imprint","IMPRINT",FACE,{"disambiguationData":[TD([[makeQuery(id+"F18.imprint","IMPRINT",EDGE,{"derivedFrom":sQuery(id+"F18.wireOp",EDGE,"E58.0")}),1.0]])]});
            var Q5;
            Q5=makeQuery(id+"F18.imprint","IMPRINT",FACE,{"disambiguationData":[TD([[makeQuery(id+"F18.imprint","IMPRINT",EDGE,{"derivedFrom":sQuery(id+"F18.wireOp",EDGE,"E67.0")}),1.0]])]});
            extrude(context, id + "F20", {"entities" : qUnion([Q0, Q1, Q2, Q3, Q4, Q5]), "operationType" : NewBodyOperationType.REMOVE, "oppositeDirection" : true, "depth" : 3.5 * mm});
        }
    });
